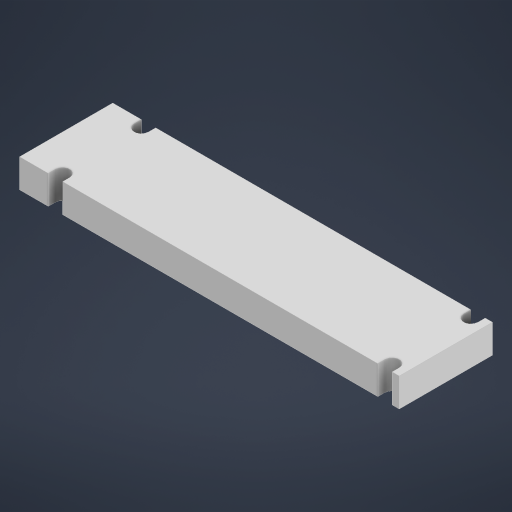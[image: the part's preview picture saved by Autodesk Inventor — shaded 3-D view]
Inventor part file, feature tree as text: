
AUTODESK INVENTOR PART (.ipt)
format: ipt  version: 2023.2 (Build 272271000, 271)  size: 223,744 bytes
history: native  units: mm
features: sketch x1
ambient origin geometry x8: Origin, YZ Plane, XZ Plane, XY Plane, X Axis, Y Axis, Z Axis, Center Point
bodies: Body1 (feature_tree)
feature tree (1):
  sketch  "Sketch1"  dims[d228=13.0mm d229=53.0mm d233=5.0mm d234=2.0mm d235=11.0mm d237=2.0mm d238=4.0mm d239=0.0mm d9=0.5mm d10=0.872665mm d11=0.5mm d12=0.872665mm d13=0.5mm d14=0.872665mm d27=0.5mm d28=0.872665mm d29=0.5mm d30=0.872665mm d88=0.5mm d89=0.872665mm d90=0.5mm d91=0.872665mm d116=0.5mm d117=0.872665mm d118=0.5mm d119=0.872665mm d154=0.5mm d155=0.872665mm d156=0.5mm d157=0.872665mm d181=0.5mm d182=0.872665mm d183=0.5mm d184=0.872665mm d221=0.5mm d222=0.872665mm d223=0.5mm d224=0.872665mm]
